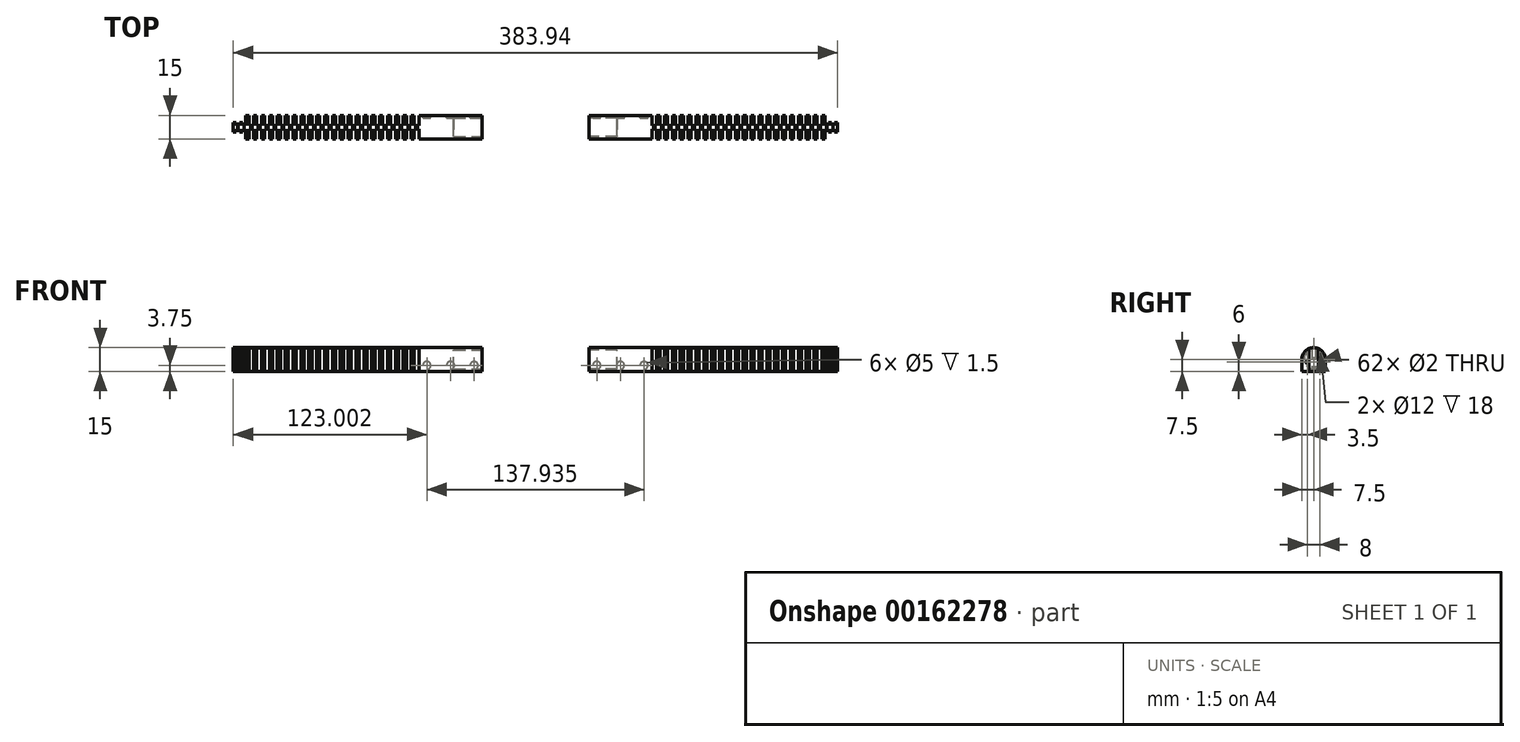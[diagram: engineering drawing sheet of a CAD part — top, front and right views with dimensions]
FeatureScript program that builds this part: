
annotation { "Feature Type Name" : "Feature", "Feature Type Description" : "" }
export const myFeature = defineFeature(function(context is Context, id is Id, definition is map)
    precondition{}
    {
        {
            var Q0;
            Q0=qCreatedBy(makeId("Top.planeOp"),FACE);
            var sketch = newSketch(context, id + "F0", { "sketchPlane" : qUnion([Q0])});
            skLineSegment(sketch, "E0", {"start": v(10.97, 0) * mm, "end": v(-254.43, 0) * mm, "construction": true});
            skLineSegment(sketch, "E1.bottom", {"start": v(-28.97, 7.5) * mm, "end": v(-178.97, 7.5) * mm});
            skLineSegment(sketch, "E1.top", {"start": v(-28.97, -7.5) * mm, "end": v(-178.97, -7.5) * mm});
            skLineSegment(sketch, "E1.left", {"start": v(-28.97, 7.5) * mm, "end": v(-28.97, -7.5) * mm});
            skLineSegment(sketch, "E1.right", {"start": v(-178.97, 7.5) * mm, "end": v(-178.97, 1) * mm});
            skPoint(sketch, "E1.middle", {"position": v(-103.97, 0) * mm});
            skLineSegment(sketch, "E2.bottom", {"start": v(-178.97, 1) * mm, "end": v(-180.97, 1) * mm});
            skLineSegment(sketch, "E2.top", {"start": v(-178.97, -1) * mm, "end": v(-180.97, -1) * mm});
            skLineSegment(sketch, "E2.right", {"start": v(-186.97, 1) * mm, "end": v(-186.97, -1) * mm});
            skLineSegment(sketch, "E3.bottom", {"start": v(-186.97, -3) * mm, "end": v(-184.97, -3) * mm});
            skLineSegment(sketch, "E3.top", {"start": v(-186.97, 3) * mm, "end": v(-184.97, 3) * mm});
            skLineSegment(sketch, "E3.left", {"start": v(-186.97, -3) * mm, "end": v(-186.97, 3) * mm});
            skLineSegment(sketch, "E3.right", {"start": v(-184.97, -3) * mm, "end": v(-184.97, -1) * mm});
            skPoint(sketch, "E4.firstSnap0", {"position": v(-182.97, -1) * mm});
            skLineSegment(sketch, "E4.bottom", {"start": v(-182.97, -3) * mm, "end": v(-180.97, -3) * mm});
            skLineSegment(sketch, "E4.top", {"start": v(-182.97, 3) * mm, "end": v(-180.97, 3) * mm});
            skLineSegment(sketch, "E4.left", {"start": v(-182.97, -3) * mm, "end": v(-182.97, -1) * mm});
            skLineSegment(sketch, "E4.right", {"start": v(-180.97, -3) * mm, "end": v(-180.97, -1) * mm});
            skLineSegment(sketch, "E5.trimOffspring", {"start": v(-178.97, -1) * mm, "end": v(-178.97, -7.5) * mm});
            skLineSegment(sketch, "E6.trimOffspring", {"start": v(-180.97, 1) * mm, "end": v(-180.97, 3) * mm});
            skLineSegment(sketch, "E7.trimOffspring", {"start": v(-182.97, 1) * mm, "end": v(-182.97, 3) * mm});
            skLineSegment(sketch, "E8.trimOffspring", {"start": v(-184.97, 1) * mm, "end": v(-184.97, 3) * mm});
            skLineSegment(sketch, "E9.trimOffspring", {"start": v(-182.97, 1) * mm, "end": v(-184.97, 1) * mm});
            skLineSegment(sketch, "E10.trimOffspring", {"start": v(-182.97, -1) * mm, "end": v(-184.97, -1) * mm});
            skSolve(sketch);
        }
        {
            var Q0;
            Q0=makeQuery(id+"F0.imprint","IMPRINT",FACE,{"disambiguationData":[TD([[makeQuery(id+"F0.imprint","IMPRINT",EDGE,{"derivedFrom":sQuery(id+"F0.wireOp",EDGE,"E1.bottom")}),1.0]])]});
            extrude(context, id + "F1", {"entities" : qUnion([Q0]), "depth" : 15 * mm});
        }
        {
            var Q0;
            Q0=makeQuery(id+"F1.opExtrude","CAP_EDGE",EDGE,{"disambiguationData":[OSD([sQuery(id+"F0.wireOp",EDGE,"E1.bottom")])],"isStart":false});
            var Q1;
            Q1=makeQuery(id+"F1.opExtrude","CAP_EDGE",EDGE,{"disambiguationData":[OSD([sQuery(id+"F0.wireOp",EDGE,"E1.top")])],"isStart":false});
            fillet(context, id + "F2", {"entities" : qUnion([Q0, Q1]), "radius" : 7.5 * mm, "tangentPropagation" : true, "allowEdgeOverflow" : false});
        }
        {
            var Q0;
            Q0=qCreatedBy(makeId("Top.planeOp"),FACE);
            var sketch = newSketch(context, id + "F3", { "sketchPlane" : qUnion([Q0])});
            skLineSegment(sketch, "E11.bottom", {"start": v(-71.97, 1) * mm, "end": v(-68.97, 1) * mm});
            skLineSegment(sketch, "E11.top", {"start": v(-71.97, 11) * mm, "end": v(-68.97, 11) * mm});
            skLineSegment(sketch, "E11.left", {"start": v(-71.97, 1) * mm, "end": v(-71.97, 11) * mm});
            skLineSegment(sketch, "E11.right", {"start": v(-68.97, 1) * mm, "end": v(-68.97, 11) * mm});
            skPoint(sketch, "E11.middle", {"position": v(-70.47, 6) * mm});
            skLineSegment(sketch, "E12.0.1.0", {"start": v(-71.97, -11) * mm, "end": v(-68.97, -11) * mm});
            skLineSegment(sketch, "E12.0.1.1", {"start": v(-71.97, -1) * mm, "end": v(-68.97, -1) * mm});
            skLineSegment(sketch, "E12.0.1.2", {"start": v(-71.97, -11) * mm, "end": v(-71.97, -1) * mm});
            skLineSegment(sketch, "E12.0.1.3", {"start": v(-68.97, -11) * mm, "end": v(-68.97, -1) * mm});
            skPoint(sketch, "E12.0.1.4", {"position": v(-70.47, -6) * mm});
            skLineSegment(sketch, "E12.1.0.0", {"start": v(-76.97, 1) * mm, "end": v(-73.97, 1) * mm});
            skLineSegment(sketch, "E12.1.0.1", {"start": v(-76.97, 11) * mm, "end": v(-73.97, 11) * mm});
            skLineSegment(sketch, "E12.1.0.2", {"start": v(-76.97, 1) * mm, "end": v(-76.97, 11) * mm});
            skLineSegment(sketch, "E12.1.0.3", {"start": v(-73.97, 1) * mm, "end": v(-73.97, 11) * mm});
            skPoint(sketch, "E12.1.0.4", {"position": v(-75.47, 6) * mm});
            skLineSegment(sketch, "E12.1.1.0", {"start": v(-76.97, -11) * mm, "end": v(-73.97, -11) * mm});
            skLineSegment(sketch, "E12.1.1.1", {"start": v(-76.97, -1) * mm, "end": v(-73.97, -1) * mm});
            skLineSegment(sketch, "E12.1.1.2", {"start": v(-76.97, -11) * mm, "end": v(-76.97, -1) * mm});
            skLineSegment(sketch, "E12.1.1.3", {"start": v(-73.97, -11) * mm, "end": v(-73.97, -1) * mm});
            skPoint(sketch, "E12.1.1.4", {"position": v(-75.47, -6) * mm});
            skLineSegment(sketch, "E12.2.0.0", {"start": v(-81.97, 1) * mm, "end": v(-78.97, 1) * mm});
            skLineSegment(sketch, "E12.2.0.1", {"start": v(-81.97, 11) * mm, "end": v(-78.97, 11) * mm});
            skLineSegment(sketch, "E12.2.0.2", {"start": v(-81.97, 1) * mm, "end": v(-81.97, 11) * mm});
            skLineSegment(sketch, "E12.2.0.3", {"start": v(-78.97, 1) * mm, "end": v(-78.97, 11) * mm});
            skPoint(sketch, "E12.2.0.4", {"position": v(-80.47, 6) * mm});
            skLineSegment(sketch, "E12.2.1.0", {"start": v(-81.97, -11) * mm, "end": v(-78.97, -11) * mm});
            skLineSegment(sketch, "E12.2.1.1", {"start": v(-81.97, -1) * mm, "end": v(-78.97, -1) * mm});
            skLineSegment(sketch, "E12.2.1.2", {"start": v(-81.97, -11) * mm, "end": v(-81.97, -1) * mm});
            skLineSegment(sketch, "E12.2.1.3", {"start": v(-78.97, -11) * mm, "end": v(-78.97, -1) * mm});
            skPoint(sketch, "E12.2.1.4", {"position": v(-80.47, -6) * mm});
            skLineSegment(sketch, "E12.3.0.0", {"start": v(-86.97, 1) * mm, "end": v(-83.97, 1) * mm});
            skLineSegment(sketch, "E12.3.0.1", {"start": v(-86.97, 11) * mm, "end": v(-83.97, 11) * mm});
            skLineSegment(sketch, "E12.3.0.2", {"start": v(-86.97, 1) * mm, "end": v(-86.97, 11) * mm});
            skLineSegment(sketch, "E12.3.0.3", {"start": v(-83.97, 1) * mm, "end": v(-83.97, 11) * mm});
            skPoint(sketch, "E12.3.0.4", {"position": v(-85.47, 6) * mm});
            skLineSegment(sketch, "E12.3.1.0", {"start": v(-86.97, -11) * mm, "end": v(-83.97, -11) * mm});
            skLineSegment(sketch, "E12.3.1.1", {"start": v(-86.97, -1) * mm, "end": v(-83.97, -1) * mm});
            skLineSegment(sketch, "E12.3.1.2", {"start": v(-86.97, -11) * mm, "end": v(-86.97, -1) * mm});
            skLineSegment(sketch, "E12.3.1.3", {"start": v(-83.97, -11) * mm, "end": v(-83.97, -1) * mm});
            skPoint(sketch, "E12.3.1.4", {"position": v(-85.47, -6) * mm});
            skLineSegment(sketch, "E12.4.0.0", {"start": v(-91.97, 1) * mm, "end": v(-88.97, 1) * mm});
            skLineSegment(sketch, "E12.4.0.1", {"start": v(-91.97, 11) * mm, "end": v(-88.97, 11) * mm});
            skLineSegment(sketch, "E12.4.0.2", {"start": v(-91.97, 1) * mm, "end": v(-91.97, 11) * mm});
            skLineSegment(sketch, "E12.4.0.3", {"start": v(-88.97, 1) * mm, "end": v(-88.97, 11) * mm});
            skPoint(sketch, "E12.4.0.4", {"position": v(-90.47, 6) * mm});
            skLineSegment(sketch, "E12.4.1.0", {"start": v(-91.97, -11) * mm, "end": v(-88.97, -11) * mm});
            skLineSegment(sketch, "E12.4.1.1", {"start": v(-91.97, -1) * mm, "end": v(-88.97, -1) * mm});
            skLineSegment(sketch, "E12.4.1.2", {"start": v(-91.97, -11) * mm, "end": v(-91.97, -1) * mm});
            skLineSegment(sketch, "E12.4.1.3", {"start": v(-88.97, -11) * mm, "end": v(-88.97, -1) * mm});
            skPoint(sketch, "E12.4.1.4", {"position": v(-90.47, -6) * mm});
            skLineSegment(sketch, "E12.5.0.0", {"start": v(-96.97, 1) * mm, "end": v(-93.97, 1) * mm});
            skLineSegment(sketch, "E12.5.0.1", {"start": v(-96.97, 11) * mm, "end": v(-93.97, 11) * mm});
            skLineSegment(sketch, "E12.5.0.2", {"start": v(-96.97, 1) * mm, "end": v(-96.97, 11) * mm});
            skLineSegment(sketch, "E12.5.0.3", {"start": v(-93.97, 1) * mm, "end": v(-93.97, 11) * mm});
            skPoint(sketch, "E12.5.0.4", {"position": v(-95.47, 6) * mm});
            skLineSegment(sketch, "E12.5.1.0", {"start": v(-96.97, -11) * mm, "end": v(-93.97, -11) * mm});
            skLineSegment(sketch, "E12.5.1.1", {"start": v(-96.97, -1) * mm, "end": v(-93.97, -1) * mm});
            skLineSegment(sketch, "E12.5.1.2", {"start": v(-96.97, -11) * mm, "end": v(-96.97, -1) * mm});
            skLineSegment(sketch, "E12.5.1.3", {"start": v(-93.97, -11) * mm, "end": v(-93.97, -1) * mm});
            skPoint(sketch, "E12.5.1.4", {"position": v(-95.47, -6) * mm});
            skLineSegment(sketch, "E12.6.0.0", {"start": v(-101.97, 1) * mm, "end": v(-98.97, 1) * mm});
            skLineSegment(sketch, "E12.6.0.1", {"start": v(-101.97, 11) * mm, "end": v(-98.97, 11) * mm});
            skLineSegment(sketch, "E12.6.0.2", {"start": v(-101.97, 1) * mm, "end": v(-101.97, 11) * mm});
            skLineSegment(sketch, "E12.6.0.3", {"start": v(-98.97, 1) * mm, "end": v(-98.97, 11) * mm});
            skPoint(sketch, "E12.6.0.4", {"position": v(-100.47, 6) * mm});
            skLineSegment(sketch, "E12.6.1.0", {"start": v(-101.97, -11) * mm, "end": v(-98.97, -11) * mm});
            skLineSegment(sketch, "E12.6.1.1", {"start": v(-101.97, -1) * mm, "end": v(-98.97, -1) * mm});
            skLineSegment(sketch, "E12.6.1.2", {"start": v(-101.97, -11) * mm, "end": v(-101.97, -1) * mm});
            skLineSegment(sketch, "E12.6.1.3", {"start": v(-98.97, -11) * mm, "end": v(-98.97, -1) * mm});
            skPoint(sketch, "E12.6.1.4", {"position": v(-100.47, -6) * mm});
            skLineSegment(sketch, "E12.7.0.0", {"start": v(-106.97, 1) * mm, "end": v(-103.97, 1) * mm});
            skLineSegment(sketch, "E12.7.0.1", {"start": v(-106.97, 11) * mm, "end": v(-103.97, 11) * mm});
            skLineSegment(sketch, "E12.7.0.2", {"start": v(-106.97, 1) * mm, "end": v(-106.97, 11) * mm});
            skLineSegment(sketch, "E12.7.0.3", {"start": v(-103.97, 1) * mm, "end": v(-103.97, 11) * mm});
            skPoint(sketch, "E12.7.0.4", {"position": v(-105.47, 6) * mm});
            skLineSegment(sketch, "E12.7.1.0", {"start": v(-106.97, -11) * mm, "end": v(-103.97, -11) * mm});
            skLineSegment(sketch, "E12.7.1.1", {"start": v(-106.97, -1) * mm, "end": v(-103.97, -1) * mm});
            skLineSegment(sketch, "E12.7.1.2", {"start": v(-106.97, -11) * mm, "end": v(-106.97, -1) * mm});
            skLineSegment(sketch, "E12.7.1.3", {"start": v(-103.97, -11) * mm, "end": v(-103.97, -1) * mm});
            skPoint(sketch, "E12.7.1.4", {"position": v(-105.47, -6) * mm});
            skLineSegment(sketch, "E12.8.0.0", {"start": v(-111.97, 1) * mm, "end": v(-108.97, 1) * mm});
            skLineSegment(sketch, "E12.8.0.1", {"start": v(-111.97, 11) * mm, "end": v(-108.97, 11) * mm});
            skLineSegment(sketch, "E12.8.0.2", {"start": v(-111.97, 1) * mm, "end": v(-111.97, 11) * mm});
            skLineSegment(sketch, "E12.8.0.3", {"start": v(-108.97, 1) * mm, "end": v(-108.97, 11) * mm});
            skPoint(sketch, "E12.8.0.4", {"position": v(-110.47, 6) * mm});
            skLineSegment(sketch, "E12.8.1.0", {"start": v(-111.97, -11) * mm, "end": v(-108.97, -11) * mm});
            skLineSegment(sketch, "E12.8.1.1", {"start": v(-111.97, -1) * mm, "end": v(-108.97, -1) * mm});
            skLineSegment(sketch, "E12.8.1.2", {"start": v(-111.97, -11) * mm, "end": v(-111.97, -1) * mm});
            skLineSegment(sketch, "E12.8.1.3", {"start": v(-108.97, -11) * mm, "end": v(-108.97, -1) * mm});
            skPoint(sketch, "E12.8.1.4", {"position": v(-110.47, -6) * mm});
            skLineSegment(sketch, "E12.9.0.0", {"start": v(-116.97, 1) * mm, "end": v(-113.97, 1) * mm});
            skLineSegment(sketch, "E12.9.0.1", {"start": v(-116.97, 11) * mm, "end": v(-113.97, 11) * mm});
            skLineSegment(sketch, "E12.9.0.2", {"start": v(-116.97, 1) * mm, "end": v(-116.97, 11) * mm});
            skLineSegment(sketch, "E12.9.0.3", {"start": v(-113.97, 1) * mm, "end": v(-113.97, 11) * mm});
            skPoint(sketch, "E12.9.0.4", {"position": v(-115.47, 6) * mm});
            skLineSegment(sketch, "E12.9.1.0", {"start": v(-116.97, -11) * mm, "end": v(-113.97, -11) * mm});
            skLineSegment(sketch, "E12.9.1.1", {"start": v(-116.97, -1) * mm, "end": v(-113.97, -1) * mm});
            skLineSegment(sketch, "E12.9.1.2", {"start": v(-116.97, -11) * mm, "end": v(-116.97, -1) * mm});
            skLineSegment(sketch, "E12.9.1.3", {"start": v(-113.97, -11) * mm, "end": v(-113.97, -1) * mm});
            skPoint(sketch, "E12.9.1.4", {"position": v(-115.47, -6) * mm});
            skLineSegment(sketch, "E12.10.0.0", {"start": v(-121.97, 1) * mm, "end": v(-118.97, 1) * mm});
            skLineSegment(sketch, "E12.10.0.1", {"start": v(-121.97, 11) * mm, "end": v(-118.97, 11) * mm});
            skLineSegment(sketch, "E12.10.0.2", {"start": v(-121.97, 1) * mm, "end": v(-121.97, 11) * mm});
            skLineSegment(sketch, "E12.10.0.3", {"start": v(-118.97, 1) * mm, "end": v(-118.97, 11) * mm});
            skPoint(sketch, "E12.10.0.4", {"position": v(-120.47, 6) * mm});
            skLineSegment(sketch, "E12.10.1.0", {"start": v(-121.97, -11) * mm, "end": v(-118.97, -11) * mm});
            skLineSegment(sketch, "E12.10.1.1", {"start": v(-121.97, -1) * mm, "end": v(-118.97, -1) * mm});
            skLineSegment(sketch, "E12.10.1.2", {"start": v(-121.97, -11) * mm, "end": v(-121.97, -1) * mm});
            skLineSegment(sketch, "E12.10.1.3", {"start": v(-118.97, -11) * mm, "end": v(-118.97, -1) * mm});
            skPoint(sketch, "E12.10.1.4", {"position": v(-120.47, -6) * mm});
            skLineSegment(sketch, "E12.11.0.0", {"start": v(-126.97, 1) * mm, "end": v(-123.97, 1) * mm});
            skLineSegment(sketch, "E12.11.0.1", {"start": v(-126.97, 11) * mm, "end": v(-123.97, 11) * mm});
            skLineSegment(sketch, "E12.11.0.2", {"start": v(-126.97, 1) * mm, "end": v(-126.97, 11) * mm});
            skLineSegment(sketch, "E12.11.0.3", {"start": v(-123.97, 1) * mm, "end": v(-123.97, 11) * mm});
            skPoint(sketch, "E12.11.0.4", {"position": v(-125.47, 6) * mm});
            skLineSegment(sketch, "E12.11.1.0", {"start": v(-126.97, -11) * mm, "end": v(-123.97, -11) * mm});
            skLineSegment(sketch, "E12.11.1.1", {"start": v(-126.97, -1) * mm, "end": v(-123.97, -1) * mm});
            skLineSegment(sketch, "E12.11.1.2", {"start": v(-126.97, -11) * mm, "end": v(-126.97, -1) * mm});
            skLineSegment(sketch, "E12.11.1.3", {"start": v(-123.97, -11) * mm, "end": v(-123.97, -1) * mm});
            skPoint(sketch, "E12.11.1.4", {"position": v(-125.47, -6) * mm});
            skLineSegment(sketch, "E12.12.0.0", {"start": v(-131.97, 1) * mm, "end": v(-128.97, 1) * mm});
            skLineSegment(sketch, "E12.12.0.1", {"start": v(-131.97, 11) * mm, "end": v(-128.97, 11) * mm});
            skLineSegment(sketch, "E12.12.0.2", {"start": v(-131.97, 1) * mm, "end": v(-131.97, 11) * mm});
            skLineSegment(sketch, "E12.12.0.3", {"start": v(-128.97, 1) * mm, "end": v(-128.97, 11) * mm});
            skPoint(sketch, "E12.12.0.4", {"position": v(-130.47, 6) * mm});
            skLineSegment(sketch, "E12.12.1.0", {"start": v(-131.97, -11) * mm, "end": v(-128.97, -11) * mm});
            skLineSegment(sketch, "E12.12.1.1", {"start": v(-131.97, -1) * mm, "end": v(-128.97, -1) * mm});
            skLineSegment(sketch, "E12.12.1.2", {"start": v(-131.97, -11) * mm, "end": v(-131.97, -1) * mm});
            skLineSegment(sketch, "E12.12.1.3", {"start": v(-128.97, -11) * mm, "end": v(-128.97, -1) * mm});
            skPoint(sketch, "E12.12.1.4", {"position": v(-130.47, -6) * mm});
            skLineSegment(sketch, "E12.13.0.0", {"start": v(-136.97, 1) * mm, "end": v(-133.97, 1) * mm});
            skLineSegment(sketch, "E12.13.0.1", {"start": v(-136.97, 11) * mm, "end": v(-133.97, 11) * mm});
            skLineSegment(sketch, "E12.13.0.2", {"start": v(-136.97, 1) * mm, "end": v(-136.97, 11) * mm});
            skLineSegment(sketch, "E12.13.0.3", {"start": v(-133.97, 1) * mm, "end": v(-133.97, 11) * mm});
            skPoint(sketch, "E12.13.0.4", {"position": v(-135.47, 6) * mm});
            skLineSegment(sketch, "E12.13.1.0", {"start": v(-136.97, -11) * mm, "end": v(-133.97, -11) * mm});
            skLineSegment(sketch, "E12.13.1.1", {"start": v(-136.97, -1) * mm, "end": v(-133.97, -1) * mm});
            skLineSegment(sketch, "E12.13.1.2", {"start": v(-136.97, -11) * mm, "end": v(-136.97, -1) * mm});
            skLineSegment(sketch, "E12.13.1.3", {"start": v(-133.97, -11) * mm, "end": v(-133.97, -1) * mm});
            skPoint(sketch, "E12.13.1.4", {"position": v(-135.47, -6) * mm});
            skLineSegment(sketch, "E12.14.0.0", {"start": v(-141.97, 1) * mm, "end": v(-138.97, 1) * mm});
            skLineSegment(sketch, "E12.14.0.1", {"start": v(-141.97, 11) * mm, "end": v(-138.97, 11) * mm});
            skLineSegment(sketch, "E12.14.0.2", {"start": v(-141.97, 1) * mm, "end": v(-141.97, 11) * mm});
            skLineSegment(sketch, "E12.14.0.3", {"start": v(-138.97, 1) * mm, "end": v(-138.97, 11) * mm});
            skPoint(sketch, "E12.14.0.4", {"position": v(-140.47, 6) * mm});
            skLineSegment(sketch, "E12.14.1.0", {"start": v(-141.97, -11) * mm, "end": v(-138.97, -11) * mm});
            skLineSegment(sketch, "E12.14.1.1", {"start": v(-141.97, -1) * mm, "end": v(-138.97, -1) * mm});
            skLineSegment(sketch, "E12.14.1.2", {"start": v(-141.97, -11) * mm, "end": v(-141.97, -1) * mm});
            skLineSegment(sketch, "E12.14.1.3", {"start": v(-138.97, -11) * mm, "end": v(-138.97, -1) * mm});
            skPoint(sketch, "E12.14.1.4", {"position": v(-140.47, -6) * mm});
            skLineSegment(sketch, "E12.15.0.0", {"start": v(-146.97, 1) * mm, "end": v(-143.97, 1) * mm});
            skLineSegment(sketch, "E12.15.0.1", {"start": v(-146.97, 11) * mm, "end": v(-143.97, 11) * mm});
            skLineSegment(sketch, "E12.15.0.2", {"start": v(-146.97, 1) * mm, "end": v(-146.97, 11) * mm});
            skLineSegment(sketch, "E12.15.0.3", {"start": v(-143.97, 1) * mm, "end": v(-143.97, 11) * mm});
            skPoint(sketch, "E12.15.0.4", {"position": v(-145.47, 6) * mm});
            skLineSegment(sketch, "E12.15.1.0", {"start": v(-146.97, -11) * mm, "end": v(-143.97, -11) * mm});
            skLineSegment(sketch, "E12.15.1.1", {"start": v(-146.97, -1) * mm, "end": v(-143.97, -1) * mm});
            skLineSegment(sketch, "E12.15.1.2", {"start": v(-146.97, -11) * mm, "end": v(-146.97, -1) * mm});
            skLineSegment(sketch, "E12.15.1.3", {"start": v(-143.97, -11) * mm, "end": v(-143.97, -1) * mm});
            skPoint(sketch, "E12.15.1.4", {"position": v(-145.47, -6) * mm});
            skLineSegment(sketch, "E12.16.0.0", {"start": v(-151.97, 1) * mm, "end": v(-148.97, 1) * mm});
            skLineSegment(sketch, "E12.16.0.1", {"start": v(-151.97, 11) * mm, "end": v(-148.97, 11) * mm});
            skLineSegment(sketch, "E12.16.0.2", {"start": v(-151.97, 1) * mm, "end": v(-151.97, 11) * mm});
            skLineSegment(sketch, "E12.16.0.3", {"start": v(-148.97, 1) * mm, "end": v(-148.97, 11) * mm});
            skPoint(sketch, "E12.16.0.4", {"position": v(-150.47, 6) * mm});
            skLineSegment(sketch, "E12.16.1.0", {"start": v(-151.97, -11) * mm, "end": v(-148.97, -11) * mm});
            skLineSegment(sketch, "E12.16.1.1", {"start": v(-151.97, -1) * mm, "end": v(-148.97, -1) * mm});
            skLineSegment(sketch, "E12.16.1.2", {"start": v(-151.97, -11) * mm, "end": v(-151.97, -1) * mm});
            skLineSegment(sketch, "E12.16.1.3", {"start": v(-148.97, -11) * mm, "end": v(-148.97, -1) * mm});
            skPoint(sketch, "E12.16.1.4", {"position": v(-150.47, -6) * mm});
            skLineSegment(sketch, "E12.17.0.0", {"start": v(-156.97, 1) * mm, "end": v(-153.97, 1) * mm});
            skLineSegment(sketch, "E12.17.0.1", {"start": v(-156.97, 11) * mm, "end": v(-153.97, 11) * mm});
            skLineSegment(sketch, "E12.17.0.2", {"start": v(-156.97, 1) * mm, "end": v(-156.97, 11) * mm});
            skLineSegment(sketch, "E12.17.0.3", {"start": v(-153.97, 1) * mm, "end": v(-153.97, 11) * mm});
            skPoint(sketch, "E12.17.0.4", {"position": v(-155.47, 6) * mm});
            skLineSegment(sketch, "E12.17.1.0", {"start": v(-156.97, -11) * mm, "end": v(-153.97, -11) * mm});
            skLineSegment(sketch, "E12.17.1.1", {"start": v(-156.97, -1) * mm, "end": v(-153.97, -1) * mm});
            skLineSegment(sketch, "E12.17.1.2", {"start": v(-156.97, -11) * mm, "end": v(-156.97, -1) * mm});
            skLineSegment(sketch, "E12.17.1.3", {"start": v(-153.97, -11) * mm, "end": v(-153.97, -1) * mm});
            skPoint(sketch, "E12.17.1.4", {"position": v(-155.47, -6) * mm});
            skLineSegment(sketch, "E12.direction1", {"start": v(-71.97, 1) * mm, "end": v(-76.97, 1) * mm, "construction": true});
            skLineSegment(sketch, "E12.direction2", {"start": v(-71.97, 1) * mm, "end": v(-71.97, -11) * mm, "construction": true});
            skLineSegment(sketch, "E13.0.18.0", {"start": v(-161.97, 1) * mm, "end": v(-158.97, 1) * mm});
            skLineSegment(sketch, "E13.3.18.0", {"start": v(-161.97, 11) * mm, "end": v(-158.97, 11) * mm});
            skLineSegment(sketch, "E13.6.18.0", {"start": v(-161.97, 1) * mm, "end": v(-161.97, 11) * mm});
            skLineSegment(sketch, "E13.9.18.0", {"start": v(-158.97, 1) * mm, "end": v(-158.97, 11) * mm});
            skPoint(sketch, "E13.12.18.0", {"position": v(-160.47, 6) * mm});
            skLineSegment(sketch, "E13.0.18.1", {"start": v(-161.97, -11) * mm, "end": v(-158.97, -11) * mm});
            skLineSegment(sketch, "E13.3.18.1", {"start": v(-161.97, -1) * mm, "end": v(-158.97, -1) * mm});
            skLineSegment(sketch, "E13.6.18.1", {"start": v(-161.97, -11) * mm, "end": v(-161.97, -1) * mm});
            skLineSegment(sketch, "E13.9.18.1", {"start": v(-158.97, -11) * mm, "end": v(-158.97, -1) * mm});
            skPoint(sketch, "E13.12.18.1", {"position": v(-160.47, -6) * mm});
            skLineSegment(sketch, "E13.0.19.0", {"start": v(-166.97, 1) * mm, "end": v(-163.97, 1) * mm});
            skLineSegment(sketch, "E13.3.19.0", {"start": v(-166.97, 11) * mm, "end": v(-163.97, 11) * mm});
            skLineSegment(sketch, "E13.6.19.0", {"start": v(-166.97, 1) * mm, "end": v(-166.97, 11) * mm});
            skLineSegment(sketch, "E13.9.19.0", {"start": v(-163.97, 1) * mm, "end": v(-163.97, 11) * mm});
            skPoint(sketch, "E13.12.19.0", {"position": v(-165.47, 6) * mm});
            skLineSegment(sketch, "E13.0.19.1", {"start": v(-166.97, -11) * mm, "end": v(-163.97, -11) * mm});
            skLineSegment(sketch, "E13.3.19.1", {"start": v(-166.97, -1) * mm, "end": v(-163.97, -1) * mm});
            skLineSegment(sketch, "E13.6.19.1", {"start": v(-166.97, -11) * mm, "end": v(-166.97, -1) * mm});
            skLineSegment(sketch, "E13.9.19.1", {"start": v(-163.97, -11) * mm, "end": v(-163.97, -1) * mm});
            skPoint(sketch, "E13.12.19.1", {"position": v(-165.47, -6) * mm});
            skLineSegment(sketch, "E13.0.20.0", {"start": v(-171.97, 1) * mm, "end": v(-168.97, 1) * mm});
            skLineSegment(sketch, "E13.3.20.0", {"start": v(-171.97, 11) * mm, "end": v(-168.97, 11) * mm});
            skLineSegment(sketch, "E13.6.20.0", {"start": v(-171.97, 1) * mm, "end": v(-171.97, 11) * mm});
            skLineSegment(sketch, "E13.9.20.0", {"start": v(-168.97, 1) * mm, "end": v(-168.97, 11) * mm});
            skPoint(sketch, "E13.12.20.0", {"position": v(-170.47, 6) * mm});
            skLineSegment(sketch, "E13.0.20.1", {"start": v(-171.97, -11) * mm, "end": v(-168.97, -11) * mm});
            skLineSegment(sketch, "E13.3.20.1", {"start": v(-171.97, -1) * mm, "end": v(-168.97, -1) * mm});
            skLineSegment(sketch, "E13.6.20.1", {"start": v(-171.97, -11) * mm, "end": v(-171.97, -1) * mm});
            skLineSegment(sketch, "E13.9.20.1", {"start": v(-168.97, -11) * mm, "end": v(-168.97, -1) * mm});
            skPoint(sketch, "E13.12.20.1", {"position": v(-170.47, -6) * mm});
            skLineSegment(sketch, "E13.0.21.0", {"start": v(-176.97, 1) * mm, "end": v(-173.97, 1) * mm});
            skLineSegment(sketch, "E13.3.21.0", {"start": v(-176.97, 11) * mm, "end": v(-173.97, 11) * mm});
            skLineSegment(sketch, "E13.6.21.0", {"start": v(-176.97, 1) * mm, "end": v(-176.97, 11) * mm});
            skLineSegment(sketch, "E13.9.21.0", {"start": v(-173.97, 1) * mm, "end": v(-173.97, 11) * mm});
            skPoint(sketch, "E13.12.21.0", {"position": v(-175.47, 6) * mm});
            skLineSegment(sketch, "E13.0.21.1", {"start": v(-176.97, -11) * mm, "end": v(-173.97, -11) * mm});
            skLineSegment(sketch, "E13.3.21.1", {"start": v(-176.97, -1) * mm, "end": v(-173.97, -1) * mm});
            skLineSegment(sketch, "E13.6.21.1", {"start": v(-176.97, -11) * mm, "end": v(-176.97, -1) * mm});
            skLineSegment(sketch, "E13.9.21.1", {"start": v(-173.97, -11) * mm, "end": v(-173.97, -1) * mm});
            skPoint(sketch, "E13.12.21.1", {"position": v(-175.47, -6) * mm});
            skSolve(sketch);
        }
        {
            var Q0;
            Q0 = qSketchRegion(id + "F3", true);
            extrude(context, id + "F4", {"entities" : qUnion([Q0]), "operationType" : NewBodyOperationType.REMOVE, "depth" : 25 * mm});
        }
        {
            var Q0;
            Q0=makeQuery(id+"F1.opExtrude","SWEPT_FACE",FACE,{"disambiguationData":[OSD([sQuery(id+"F0.wireOp",EDGE,"E1.left")])]});
            var sketch = newSketch(context, id + "F5", { "sketchPlane" : qUnion([Q0])});
            skCircle(sketch, "E14", {"center": v(0, 7.5) * mm, "radius": 6 * mm});
            skSolve(sketch);
        }
        {
            var Q0;
            Q0 = qSketchRegion(id + "F5", true);
            extrude(context, id + "F6", {"entities" : qUnion([Q0]), "operationType" : NewBodyOperationType.REMOVE, "oppositeDirection" : true, "depth" : 18 * mm});
        }
        {
            var Q0;
            {var subQ0=sQuery(id+"F0.wireOp",EDGE,"E1.left");var subQ2=sQuery(id+"F0.wireOp",EDGE,"E1.bottom");Q0=makeQuery(id+"F4.boolean.opBoolean","SPLIT",FACE,{"disambiguationData":[TD([makeQuery(id+"F1.opExtrude","SWEPT_FACE",FACE,{"disambiguationData":[OSD([subQ0])]})])],"derivedFrom":makeQuery(id+"F1.opExtrude","SWEPT_FACE",FACE,{"disambiguationData":[OSD([subQ2])]})});}
            var sketch = newSketch(context, id + "F7", { "sketchPlane" : qUnion([Q0])});
            skCircle(sketch, "E15", {"center": v(33.97, 3.75) * mm, "radius": 2.5 * mm});
            skCircle(sketch, "E16", {"center": v(63.97, 3.75) * mm, "radius": 2.5 * mm});
            skLineSegment(sketch, "E17", {"start": v(28.97, 3.75) * mm, "end": v(68.97, 3.75) * mm, "construction": true});
            skCircle(sketch, "E18", {"center": v(48.97, 3.75) * mm, "radius": 2.5 * mm});
            skSolve(sketch);
        }
        {
            var Q0;
            Q0 = qSketchRegion(id + "F7", true);
            extrude(context, id + "F8", {"entities" : qUnion([Q0]), "operationType" : NewBodyOperationType.REMOVE, "oppositeDirection" : true, "depth" : 1.5 * mm});
        }
        {
            var Q0;
            Q0=qCreatedBy(makeId("Right.planeOp"),FACE);
            cPlane(context, id + "F9", {"entities" : qUnion([Q0]), "cplaneType" : CPlaneType.OFFSET, "offset" : 5 * mm, "width" : 150 * mm, "height" : 150 * mm});
        }
        {
            var Q0;
            Q0=makeQuery(id+"F1.opExtrude","SWEPT_FACE",FACE,{"disambiguationData":[OSD([sQuery(id+"F0.wireOp",EDGE,"E1.right")])]});
            var sketch = newSketch(context, id + "F10", { "sketchPlane" : qUnion([Q0])});
            skCircle(sketch, "E19", {"center": v(4, 6) * mm, "radius": 1 * mm});
            skSolve(sketch);
        }
        {
            var Q0;
            Q0 = qSketchRegion(id + "F10", true);
            extrude(context, id + "F11", {"entities" : qUnion([Q0]), "operationType" : NewBodyOperationType.REMOVE, "oppositeDirection" : true, "depth" : 45 * mm});
        }
        {
            var Q0;
            Q0=makeQuery(id+"F1.opExtrude","SWEPT_FACE",FACE,{"disambiguationData":[OSD([sQuery(id+"F0.wireOp",EDGE,"E1.right")])]});
            var sketch = newSketch(context, id + "F12", { "sketchPlane" : qUnion([Q0])});
            skCircle(sketch, "E20", {"center": v(-4, 6) * mm, "radius": 1 * mm});
            skSolve(sketch);
        }
        {
            var Q0;
            Q0 = qSketchRegion(id + "F12", true);
            extrude(context, id + "F13", {"entities" : qUnion([Q0]), "operationType" : NewBodyOperationType.REMOVE, "oppositeDirection" : true, "depth" : 110 * mm});
        }
        {
            var Q0;
            Q0=makeQuery(id+"F1.opExtrude","SWEPT_BODY",BODY,{"disambiguationData":[OSD([sQuery(id+"F0.wireOp",EDGE,"E1.bottom"),sQuery(id+"F0.wireOp",EDGE,"E1.top"),sQuery(id+"F0.wireOp",EDGE,"E1.left"),sQuery(id+"F0.wireOp",EDGE,"E1.right")])]});
            var Q1;
            Q1=qCreatedBy(id+"F9.planeOp",FACE);
            mirror(context, id + "F14", {"entities" : qUnion([Q0]), "mirrorPlane" : qUnion([Q1])});
        }
    });
